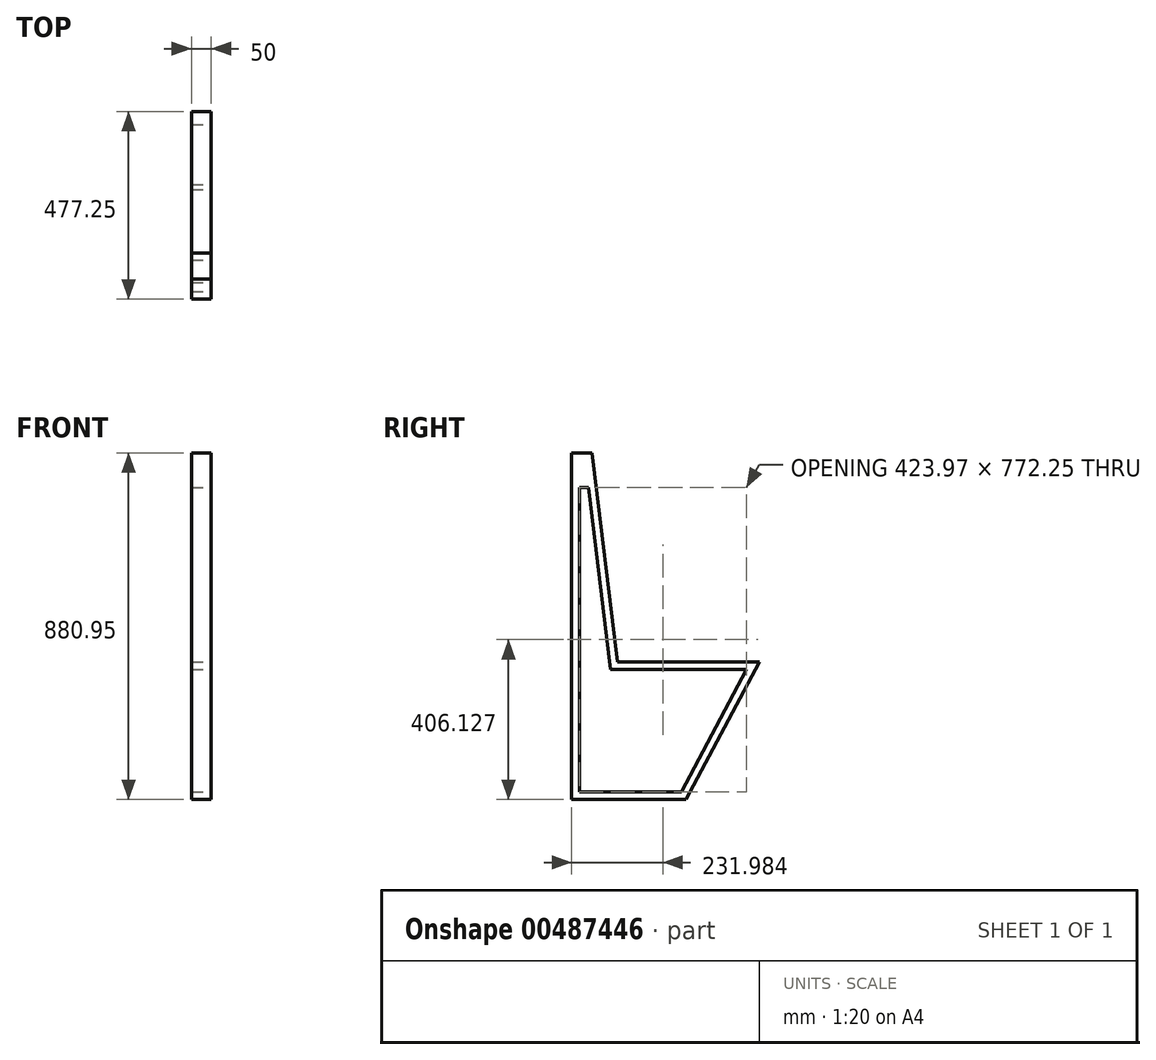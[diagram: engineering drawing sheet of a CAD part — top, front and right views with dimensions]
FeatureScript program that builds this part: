
annotation { "Feature Type Name" : "Feature", "Feature Type Description" : "" }
export const myFeature = defineFeature(function(context is Context, id is Id, definition is map)
    precondition{}
    {
        {
            var Q0;
            Q0=qCreatedBy(makeId("Right.planeOp"),FACE);
            var sketch = newSketch(context, id + "F0", { "sketchPlane" : qUnion([Q0])});
            skLineSegment(sketch, "E0", {"start": v(477.25, 350) * mm, "end": v(117.25, 350) * mm});
            skLineSegment(sketch, "E1", {"start": v(477.25, 350) * mm, "end": v(291.24, 0) * mm});
            skLineSegment(sketch, "E2", {"start": v(291.24, 0) * mm, "end": v(0, 0) * mm});
            skLineSegment(sketch, "E3", {"start": v(0, 0) * mm, "end": v(0, 880.95) * mm});
            skLineSegment(sketch, "E4", {"start": v(0, 880.95) * mm, "end": v(52.05, 880.95) * mm});
            skLineSegment(sketch, "E5", {"start": v(117.25, 350) * mm, "end": v(52.05, 880.95) * mm});
            skLineSegment(sketch, "E6.0", {"start": v(20, 20) * mm, "end": v(20, 792.25) * mm});
            skLineSegment(sketch, "E6.1", {"start": v(99.55, 330) * mm, "end": v(42.8, 792.25) * mm});
            skLineSegment(sketch, "E6.2", {"start": v(443.97, 330) * mm, "end": v(99.55, 330) * mm});
            skLineSegment(sketch, "E6.3", {"start": v(443.97, 330) * mm, "end": v(279.22, 20) * mm});
            skLineSegment(sketch, "E6.4", {"start": v(279.22, 20) * mm, "end": v(20, 20) * mm});
            skLineSegment(sketch, "E7", {"start": v(20, 792.25) * mm, "end": v(42.8, 792.25) * mm});
            skSolve(sketch);
        }
        {
            var Q0;
            Q0=qSketchRegion(id+"F0",true);
            extrude(context, id + "F1", {"entities" : qUnion([Q0]), "oppositeDirection" : true, "depth" : 50 * mm});
        }
    });
